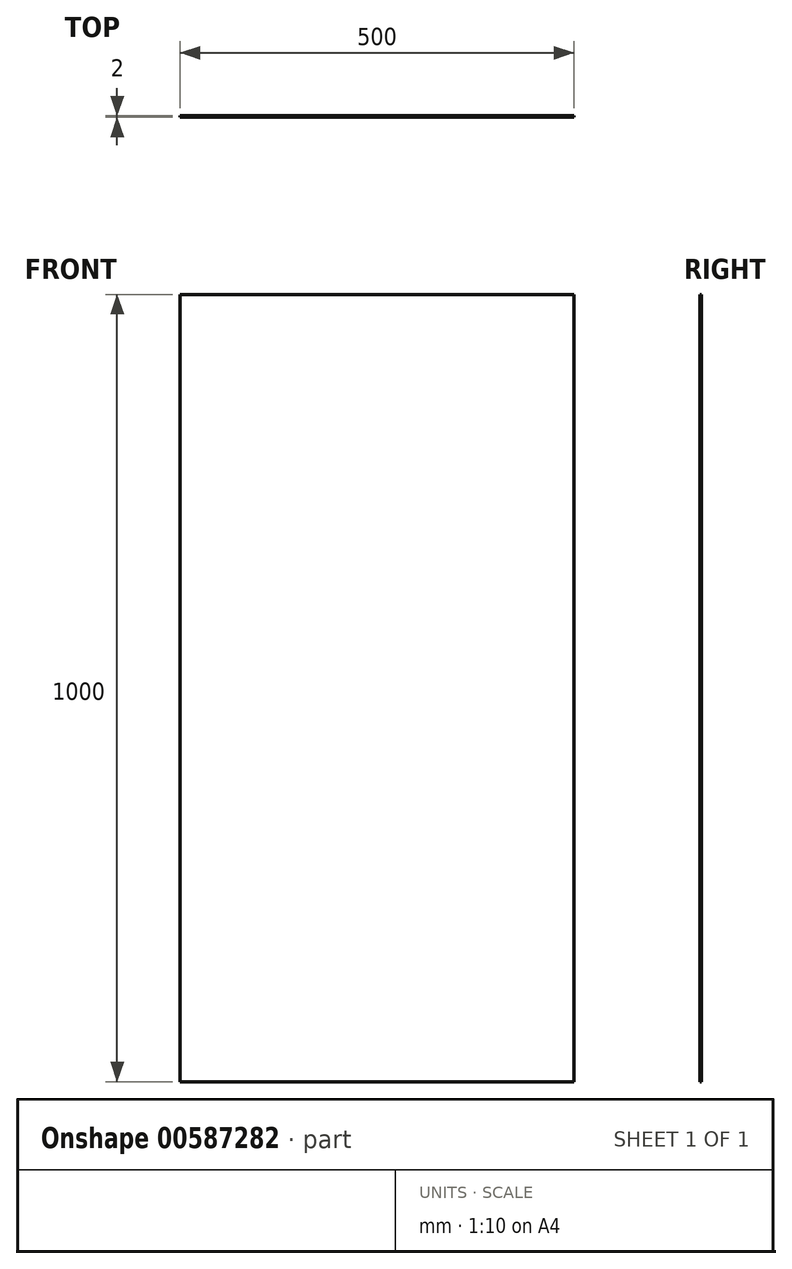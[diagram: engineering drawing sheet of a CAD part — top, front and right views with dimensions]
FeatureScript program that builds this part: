
annotation { "Feature Type Name" : "Feature", "Feature Type Description" : "" }
export const myFeature = defineFeature(function(context is Context, id is Id, definition is map)
    precondition{}
    {
        {
            var Q0;
            Q0=qCreatedBy(makeId("Front.planeOp"),FACE);
            var sketch = newSketch(context, id + "F0", { "sketchPlane" : qUnion([Q0])});
            skLineSegment(sketch, "E0.bottom", {"start": v(250, 500) * mm, "end": v(-250, 500) * mm});
            skLineSegment(sketch, "E0.top", {"start": v(250, -500) * mm, "end": v(-250, -500) * mm});
            skLineSegment(sketch, "E0.left", {"start": v(250, 500) * mm, "end": v(250, -500) * mm});
            skLineSegment(sketch, "E0.right", {"start": v(-250, 500) * mm, "end": v(-250, -500) * mm});
            skPoint(sketch, "E0.middle", {"position": v(0, 0) * mm});
            skSolve(sketch);
        }
        {
            var Q0;
            Q0=makeQuery(id+"F0.imprint","IMPRINT",FACE,{"disambiguationData":[TD([[makeQuery(id+"F0.imprint","IMPRINT",EDGE,{"derivedFrom":sQuery(id+"F0.wireOp",EDGE,"E0.bottom")}),1.0]])]});
            extrude(context, id + "F1", {"entities" : qUnion([Q0]), "depth" : 2 * mm, "offsetDistance" : 25 * mm});
        }
    });
